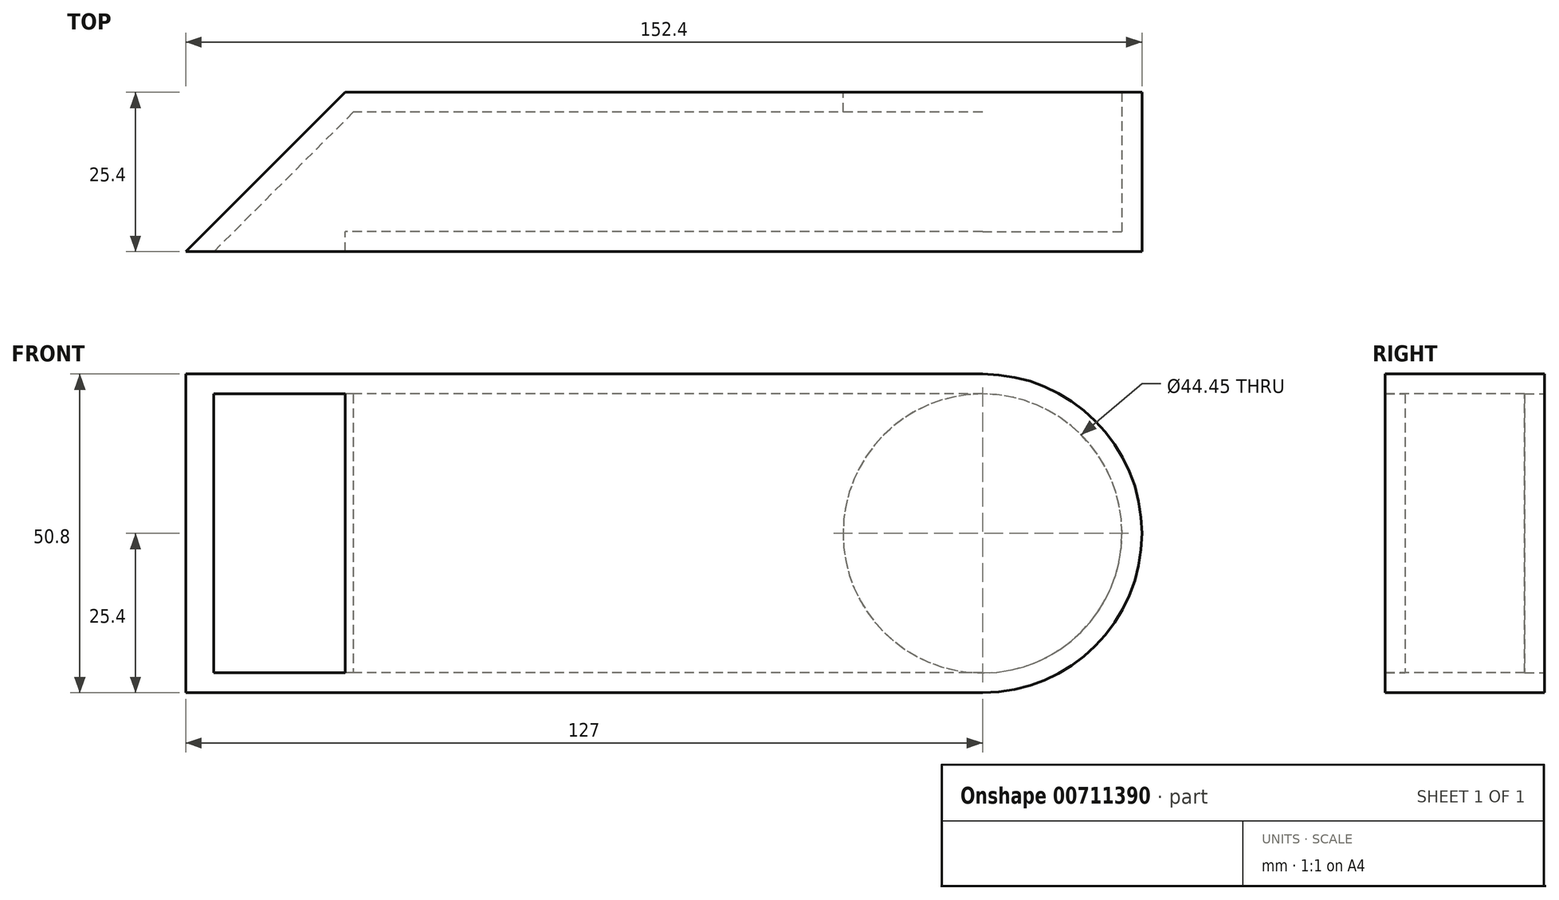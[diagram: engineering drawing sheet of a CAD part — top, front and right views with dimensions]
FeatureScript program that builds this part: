
annotation { "Feature Type Name" : "Feature", "Feature Type Description" : "" }
export const myFeature = defineFeature(function(context is Context, id is Id, definition is map)
    precondition{}
    {
        {
            var Q0;
            Q0=qCreatedBy(makeId("Front.planeOp"),FACE);
            var sketch = newSketch(context, id + "F0", { "sketchPlane" : qUnion([Q0])});
            skCircle(sketch, "E0", {"center": v(0, 0) * mm, "radius": 25.4 * mm});
            skSolve(sketch);
        }
        {
            var Q0;
            Q0 = qSketchRegion(id + "F0", true);
            extrude(context, id + "F1", {"entities" : qUnion([Q0]), "oppositeDirection" : true, "depth" : 25.4 * mm, "offsetDistance" : 25.4 * mm});
        }
        {
            var Q0;
            Q0=qCreatedBy(makeId("Right.planeOp"),FACE);
            var sketch = newSketch(context, id + "F2", { "sketchPlane" : qUnion([Q0])});
            skLineSegment(sketch, "E1.bottom", {"start": v(0, 25.4) * mm, "end": v(25.4, 25.4) * mm});
            skLineSegment(sketch, "E1.top", {"start": v(0, -25.4) * mm, "end": v(25.4, -25.4) * mm});
            skLineSegment(sketch, "E1.left", {"start": v(0, 25.4) * mm, "end": v(0, -25.4) * mm});
            skLineSegment(sketch, "E1.right", {"start": v(25.4, 25.4) * mm, "end": v(25.4, -25.4) * mm});
            skSolve(sketch);
        }
        {
            var Q0;
            Q0 = qSketchRegion(id + "F2", true);
            extrude(context, id + "F3", {"entities" : qUnion([Q0]), "operationType" : NewBodyOperationType.ADD, "oppositeDirection" : true, "depth" : 101.6 * mm, "offsetDistance" : 25.4 * mm});
        }
        {
            var Q0;
            Q0=makeQuery(id+"F3.opExtrude","CAP_FACE",FACE,{"disambiguationData":[OSD([sQuery(id+"F2.wireOp",EDGE,"E1.bottom"),sQuery(id+"F2.wireOp",EDGE,"E1.top"),sQuery(id+"F2.wireOp",EDGE,"E1.left"),sQuery(id+"F2.wireOp",EDGE,"E1.right")])],"isStart":false});
            var sketch = newSketch(context, id + "F4", { "sketchPlane" : qUnion([Q0])});
            skLineSegment(sketch, "E2.bottom", {"start": v(-22.22, 22.23) * mm, "end": v(-3.17, 22.23) * mm});
            skLineSegment(sketch, "E2.top", {"start": v(-22.22, -22.23) * mm, "end": v(-3.17, -22.22) * mm});
            skLineSegment(sketch, "E2.left", {"start": v(-22.22, 22.23) * mm, "end": v(-22.22, -22.23) * mm});
            skLineSegment(sketch, "E2.right", {"start": v(-3.17, 22.23) * mm, "end": v(-3.17, -22.22) * mm});
            skSolve(sketch);
        }
        {
            var Q0;
            Q0 = qSketchRegion(id + "F4", true);
            extrude(context, id + "F5", {"entities" : qUnion([Q0]), "operationType" : NewBodyOperationType.REMOVE, "oppositeDirection" : true, "depth" : 101.6 * mm, "offsetDistance" : 25.4 * mm});
        }
        {
            var Q0;
            Q0=makeQuery(id+"F3.boolean.opBoolean","MERGE",FACE,{"derivedFrom":[makeQuery(id+"F1.opExtrude","CAP_FACE",FACE,{"disambiguationData":[OSD([sQuery(id+"F0.wireOp",EDGE,"E0")])],"isStart":false}),makeQuery(id+"F3.opExtrude","SWEPT_FACE",FACE,{"disambiguationData":[OSD([sQuery(id+"F2.wireOp",EDGE,"E1.right")])]})]});
            var sketch = newSketch(context, id + "F6", { "sketchPlane" : qUnion([Q0])});
            skCircle(sketch, "E3", {"center": v(0, 0) * mm, "radius": 22.22 * mm});
            skSolve(sketch);
        }
        {
            var Q0;
            Q0 = qSketchRegion(id + "F6", true);
            extrude(context, id + "F7", {"entities" : qUnion([Q0]), "operationType" : NewBodyOperationType.REMOVE, "oppositeDirection" : true, "depth" : 22.22 * mm, "offsetDistance" : 25.4 * mm});
        }
        {
            var Q0;
            Q0=makeQuery(id+"F3.opExtrude","SWEPT_FACE",FACE,{"disambiguationData":[OSD([sQuery(id+"F2.wireOp",EDGE,"E1.top")])]});
            var sketch = newSketch(context, id + "F8", { "sketchPlane" : qUnion([Q0])});
            skLineSegment(sketch, "E4", {"start": v(-101.6, -25.4) * mm, "end": v(-127, 0) * mm});
            skLineSegment(sketch, "E5", {"start": v(-127, 0) * mm, "end": v(-101.6, 0) * mm});
            skLineSegment(sketch, "E6", {"start": v(-101.6, 0) * mm, "end": v(-101.6, -25.4) * mm});
            skSolve(sketch);
        }
        {
            var Q0;
            Q0 = qSketchRegion(id + "F8", true);
            extrude(context, id + "F9", {"entities" : qUnion([Q0]), "operationType" : NewBodyOperationType.ADD, "oppositeDirection" : true, "depth" : 3.17 * mm, "offsetDistance" : 25.4 * mm});
        }
        {
            var Q0;
            Q0=makeQuery(id+"F3.opExtrude","SWEPT_FACE",FACE,{"disambiguationData":[OSD([sQuery(id+"F2.wireOp",EDGE,"E1.bottom")])]});
            var sketch = newSketch(context, id + "F10", { "sketchPlane" : qUnion([Q0])});
            skLineSegment(sketch, "E7", {"start": v(-101.6, 25.4) * mm, "end": v(-127, 0) * mm});
            skLineSegment(sketch, "E8", {"start": v(-127, 0) * mm, "end": v(-101.6, 0) * mm});
            skLineSegment(sketch, "E9", {"start": v(-101.6, 0) * mm, "end": v(-101.6, 25.4) * mm});
            skSolve(sketch);
        }
        {
            var Q0;
            Q0 = qSketchRegion(id + "F10", true);
            extrude(context, id + "F11", {"entities" : qUnion([Q0]), "operationType" : NewBodyOperationType.ADD, "oppositeDirection" : true, "depth" : 3.17 * mm, "offsetDistance" : 25.4 * mm});
        }
        {
            var Q0;
            Q0=makeQuery(id+"F11.boolean.opBoolean","MERGE",FACE,{"derivedFrom":[makeQuery(id+"F3.opExtrude","SWEPT_FACE",FACE,{"disambiguationData":[OSD([sQuery(id+"F2.wireOp",EDGE,"E1.bottom")])]}),makeQuery(id+"F11.opExtrude","CAP_FACE",FACE,{"disambiguationData":[OSD([sQuery(id+"F10.wireOp",EDGE,"9OJXiMaq-sjmX-vpTJ-fd7s-740GWeuJO5Wi"),sQuery(id+"F10.wireOp",EDGE,"z7p4yIt7-naRR-9Lwj-Mzls-5dgwCY9Kb7bQ"),sQuery(id+"F10.wireOp",EDGE,"xpV1WHHW-PRpI-mdVa-5A5S-gn6efholyh6H")])],"isStart":true})]});
            var sketch = newSketch(context, id + "F12", { "sketchPlane" : qUnion([Q0])});
            skLineSegment(sketch, "E10", {"start": v(-101.6, 25.4) * mm, "end": v(-127, 0) * mm});
            skLineSegment(sketch, "E11", {"start": v(-127, 0) * mm, "end": v(-122.5, 0) * mm});
            skLineSegment(sketch, "E12", {"start": v(-122.5, 0) * mm, "end": v(-97.1, 25.4) * mm});
            skLineSegment(sketch, "E13", {"start": v(-97.1, 25.4) * mm, "end": v(-101.6, 25.4) * mm});
            skSolve(sketch);
        }
        {
            var Q0;
            Q0 = qSketchRegion(id + "F12", true);
            extrude(context, id + "F13", {"entities" : qUnion([Q0]), "operationType" : NewBodyOperationType.ADD, "oppositeDirection" : true, "depth" : 50.8 * mm, "offsetDistance" : 25.4 * mm});
        }
    });
